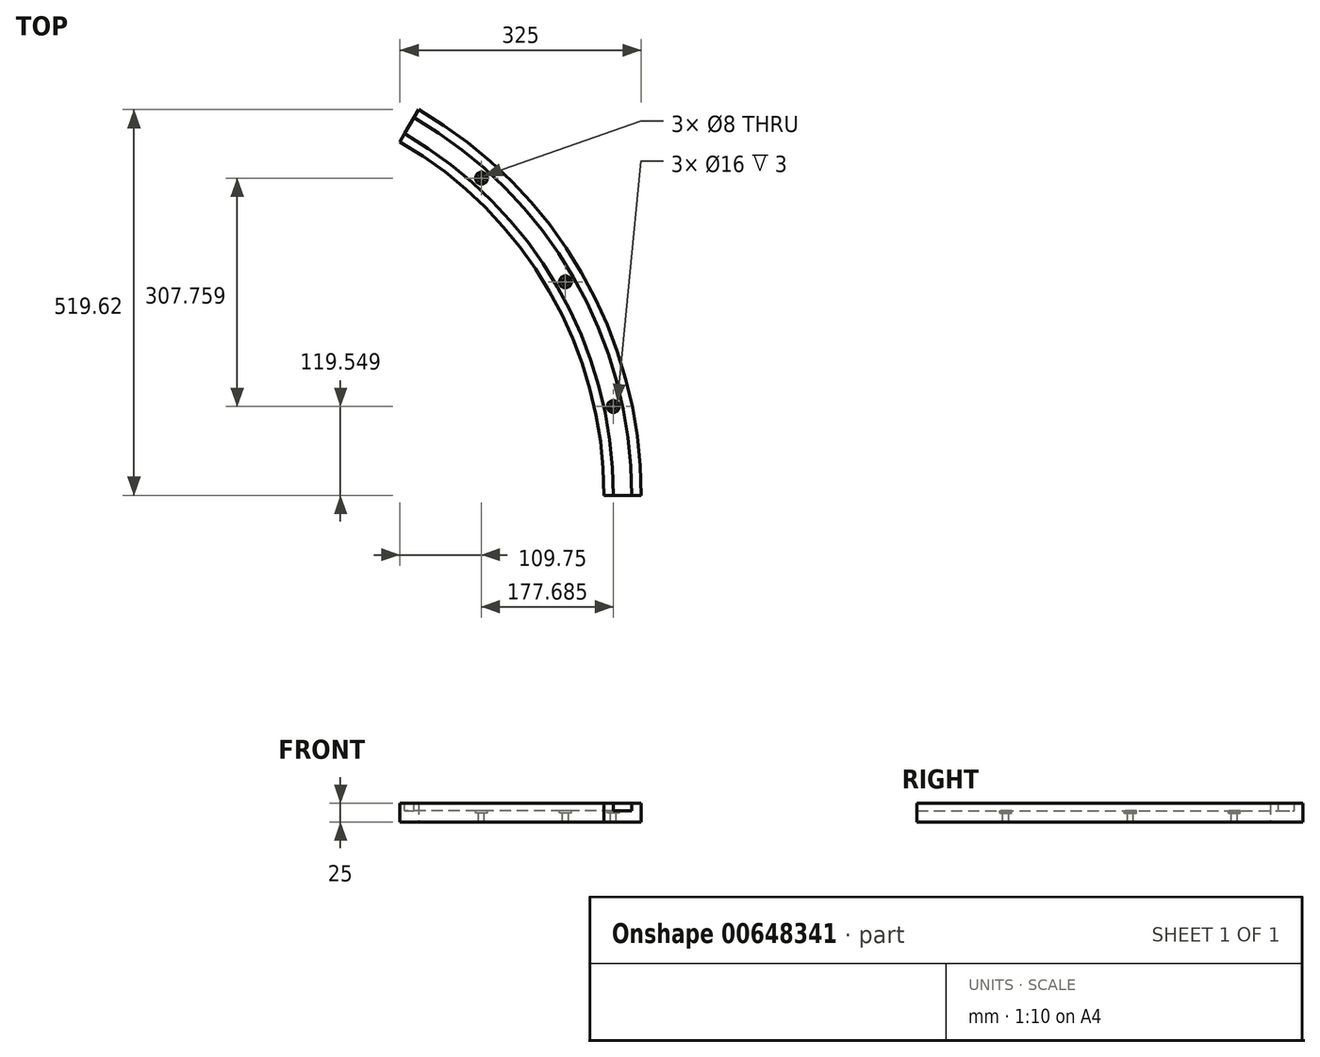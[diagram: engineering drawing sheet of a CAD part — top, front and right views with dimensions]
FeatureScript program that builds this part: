
annotation { "Feature Type Name" : "Feature", "Feature Type Description" : "" }
export const myFeature = defineFeature(function(context is Context, id is Id, definition is map)
    precondition{}
    {
        {
            var Q0;
            Q0=qCreatedBy(makeId("Top.planeOp"),FACE);
            var sketch = newSketch(context, id + "F0", { "sketchPlane" : qUnion([Q0])});
            skCircle(sketch, "E0", {"center": v(0, 0) * mm, "radius": 600 * mm, "construction": true});
            skCircle(sketch, "E1.0", {"center": v(0, 0) * mm, "radius": 550 * mm, "construction": true});
            skLineSegment(sketch, "E2", {"start": v(0, 0) * mm, "end": v(600, 0) * mm, "construction": true});
            skLineSegment(sketch, "E3", {"start": v(0, 0) * mm, "end": v(300, 519.62) * mm, "construction": true});
            skArc(sketch, "E4", {"start": v(275, 476.31) * mm, "mid": v(476.31, 275) * mm, "end": v(550, 0) * mm});
            skArc(sketch, "E5", {"start": v(300, 519.62) * mm, "mid": v(519.62, 300) * mm, "end": v(600, 0) * mm});
            skLineSegment(sketch, "E6", {"start": v(550, 0) * mm, "end": v(600, 0) * mm});
            skLineSegment(sketch, "E7", {"start": v(275, 476.31) * mm, "end": v(300, 519.62) * mm});
            skSolve(sketch);
        }
        {
            var Q0;
            Q0 = qSketchRegion(id + "F0", true);
            extrude(context, id + "F1", {"entities" : qUnion([Q0]), "depth" : 25 * mm, "offsetDistance" : 25 * mm});
        }
        {
            var Q0;
            Q0=makeQuery(id+"F1.opExtrude","CAP_FACE",FACE,{"disambiguationData":[OSD([sQuery(id+"F0.wireOp",EDGE,"E4"),sQuery(id+"F0.wireOp",EDGE,"E5"),sQuery(id+"F0.wireOp",EDGE,"E6"),sQuery(id+"F0.wireOp",EDGE,"E7")])],"isStart":false});
            var sketch = newSketch(context, id + "F2", { "sketchPlane" : qUnion([Q0])});
            skArc(sketch, "E8.0", {"start": v(281.25, 487.14) * mm, "mid": v(487.14, 281.25) * mm, "end": v(562.5, 0) * mm});
            skArc(sketch, "E9.0", {"start": v(293.75, 508.79) * mm, "mid": v(508.79, 293.75) * mm, "end": v(587.5, 0) * mm});
            skLineSegment(sketch, "E10", {"start": v(562.5, 0) * mm, "end": v(587.5, 0) * mm});
            skLineSegment(sketch, "E11", {"start": v(281.25, 487.14) * mm, "end": v(293.75, 508.79) * mm});
            skSolve(sketch);
        }
        {
            var Q0;
            Q0 = qSketchRegion(id + "F2", true);
            extrude(context, id + "F3", {"entities" : qUnion([Q0]), "operationType" : NewBodyOperationType.REMOVE, "oppositeDirection" : true, "depth" : 10 * mm, "offsetDistance" : 25 * mm});
        }
        {
            var Q0;
            Q0=makeQuery(id+"F3.boolean.opBoolean","COPY",FACE,{"derivedFrom":makeQuery(id+"F3.opExtrude","CAP_FACE",FACE,{"disambiguationData":[OSD([sQuery(id+"F2.wireOp",EDGE,"E8.0"),sQuery(id+"F2.wireOp",EDGE,"E9.0"),sQuery(id+"F2.wireOp",EDGE,"E10"),sQuery(id+"F2.wireOp",EDGE,"E11")])],"isStart":false})});
            var sketch = newSketch(context, id + "F4", { "sketchPlane" : qUnion([Q0])});
            skLineSegment(sketch, "E12", {"start": v(487.14, 281.25) * mm, "end": v(508.79, 293.75) * mm, "construction": true});
            skPoint(sketch, "E13", {"position": v(497.96, 287.5) * mm});
            skLineSegment(sketch, "E14", {"start": v(0, 0) * mm, "end": v(393.11, 436.6) * mm, "construction": true});
            skLineSegment(sketch, "E15", {"start": v(0, 0) * mm, "end": v(574.66, 122.15) * mm, "construction": true});
            skLineSegment(sketch, "E16", {"start": v(393.11, 436.6) * mm, "end": v(376.39, 418.02) * mm});
            skLineSegment(sketch, "E17", {"start": v(574.66, 122.15) * mm, "end": v(550.2, 116.95) * mm});
            skPoint(sketch, "E18", {"position": v(562.43, 119.55) * mm});
            skPoint(sketch, "E19", {"position": v(384.75, 427.3) * mm});
            skPoint(sketch, "E20", {"position": v(448.16, 421.3) * mm});
            skSolve(sketch);
        }
        {
            var Q0;
            Q0=sQuery(id+"F4.wireOp",VERTEX,"E13");
            var Q1;
            Q1=sQuery(id+"F4.wireOp",VERTEX,"E19");
            var Q2;
            Q2=sQuery(id+"F4.wireOp",VERTEX,"E18");
            var Q3;
            Q3=makeQuery(id+"F1.opExtrude","SWEPT_BODY",BODY,{"disambiguationData":[OSD([sQuery(id+"F0.wireOp",EDGE,"E4"),sQuery(id+"F0.wireOp",EDGE,"E5"),sQuery(id+"F0.wireOp",EDGE,"E6"),sQuery(id+"F0.wireOp",EDGE,"E7")])]});
            hole(context, id + "F5", {"style" : HoleStyle.C_BORE, "endStyle" : HoleEndStyle.THROUGH, "holeDiameter" : 8 * mm, "cBoreDiameter" : 16 * mm, "cBoreDepth" : 3 * mm, "majorDiameter" : 5 * mm, "isTappedThrough" : true, "tappedDepth" : 12 * mm, "tapClearance" : 3, "locations" : qUnion([Q0, Q1, Q2]), "scope" : qUnion([Q3])});
        }
    });
